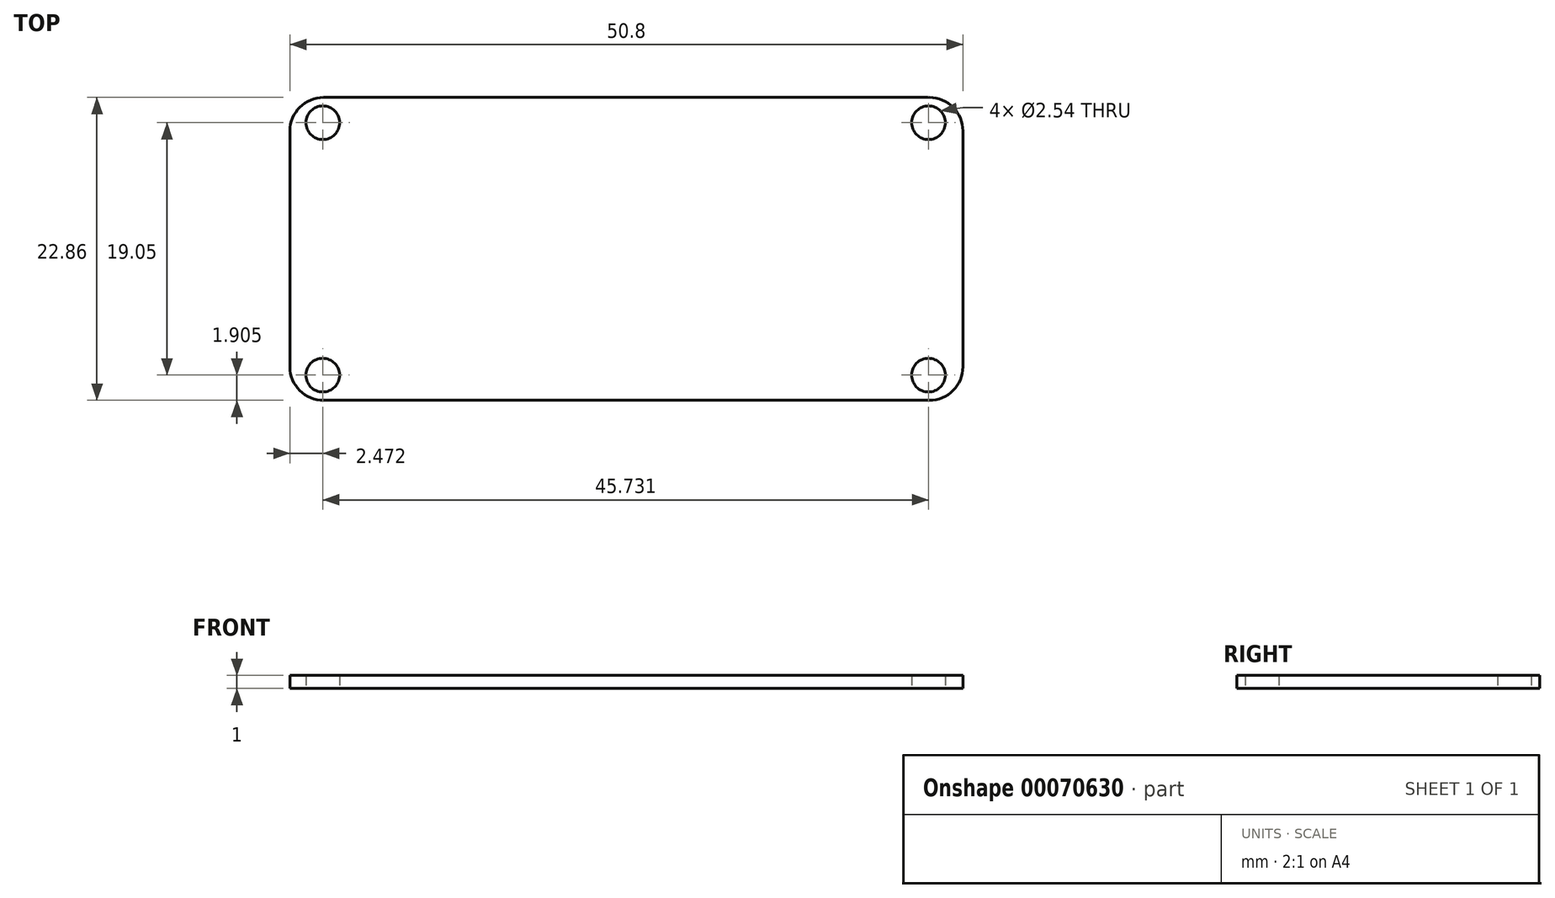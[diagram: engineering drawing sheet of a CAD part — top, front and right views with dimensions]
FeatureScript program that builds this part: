
annotation { "Feature Type Name" : "Feature", "Feature Type Description" : "" }
export const myFeature = defineFeature(function(context is Context, id is Id, definition is map)
    precondition{}
    {
        {
            var Q0;
            Q0=qCreatedBy(makeId("Top.planeOp"),FACE);
            var sketch = newSketch(context, id + "F0", { "sketchPlane" : qUnion([Q0])});
            skLineSegment(sketch, "E0.bottom", {"start": v(-22.86, 11.43) * mm, "end": v(22.86, 11.43) * mm});
            skLineSegment(sketch, "E0.top", {"start": v(-22.86, -11.43) * mm, "end": v(22.86, -11.43) * mm});
            skLineSegment(sketch, "E0.left", {"start": v(-25.4, 8.89) * mm, "end": v(-25.4, -8.89) * mm});
            skLineSegment(sketch, "E0.right", {"start": v(25.4, 8.89) * mm, "end": v(25.4, -8.89) * mm});
            skCircle(sketch, "E1", {"center": v(-22.92, 9.52) * mm, "radius": 1.27 * mm});
            skCircle(sketch, "E2.1.0.0", {"center": v(22.8, 9.52) * mm, "radius": 1.27 * mm});
            skLineSegment(sketch, "E2.direction1", {"start": v(-22.92, 9.52) * mm, "end": v(22.8, 9.52) * mm, "construction": true});
            skCircle(sketch, "E3.1.0.0", {"center": v(22.8, -9.52) * mm, "radius": 1.27 * mm});
            skCircle(sketch, "E3.1.0.1", {"center": v(-22.93, -9.52) * mm, "radius": 1.27 * mm});
            skLineSegment(sketch, "E3.direction1", {"start": v(22.8, 9.52) * mm, "end": v(22.8, -9.52) * mm, "construction": true});
            skPoint(sketch, "E4.visualSharp", {"position": v(-25.4, 11.43) * mm});
            skArc(sketch, "E4.filletArc", {"start": v(-22.86, 11.43) * mm, "mid": v(-24.66, 10.69) * mm, "end": v(-25.4, 8.89) * mm});
            skPoint(sketch, "E5.visualSharp", {"position": v(25.4, 11.43) * mm});
            skArc(sketch, "E5.filletArc", {"start": v(25.4, 8.89) * mm, "mid": v(24.66, 10.69) * mm, "end": v(22.86, 11.43) * mm});
            skPoint(sketch, "E6.visualSharp", {"position": v(-25.4, -11.43) * mm});
            skArc(sketch, "E6.filletArc", {"start": v(-25.4, -8.89) * mm, "mid": v(-24.66, -10.69) * mm, "end": v(-22.86, -11.43) * mm});
            skPoint(sketch, "E7.visualSharp", {"position": v(25.4, -11.43) * mm});
            skArc(sketch, "E7.filletArc", {"start": v(22.86, -11.43) * mm, "mid": v(24.66, -10.69) * mm, "end": v(25.4, -8.89) * mm});
            skSolve(sketch);
        }
        {
            var Q0;
            Q0=makeQuery(id+"F0.imprint","IMPRINT",FACE,{"disambiguationData":[TD([[makeQuery(id+"F0.imprint","IMPRINT",EDGE,{"derivedFrom":sQuery(id+"F0.wireOp",EDGE,"E0.bottom")}),-1.0]])]});
            extrude(context, id + "F1", {"entities" : qUnion([Q0]), "depth" : 1 * mm});
        }
    });
